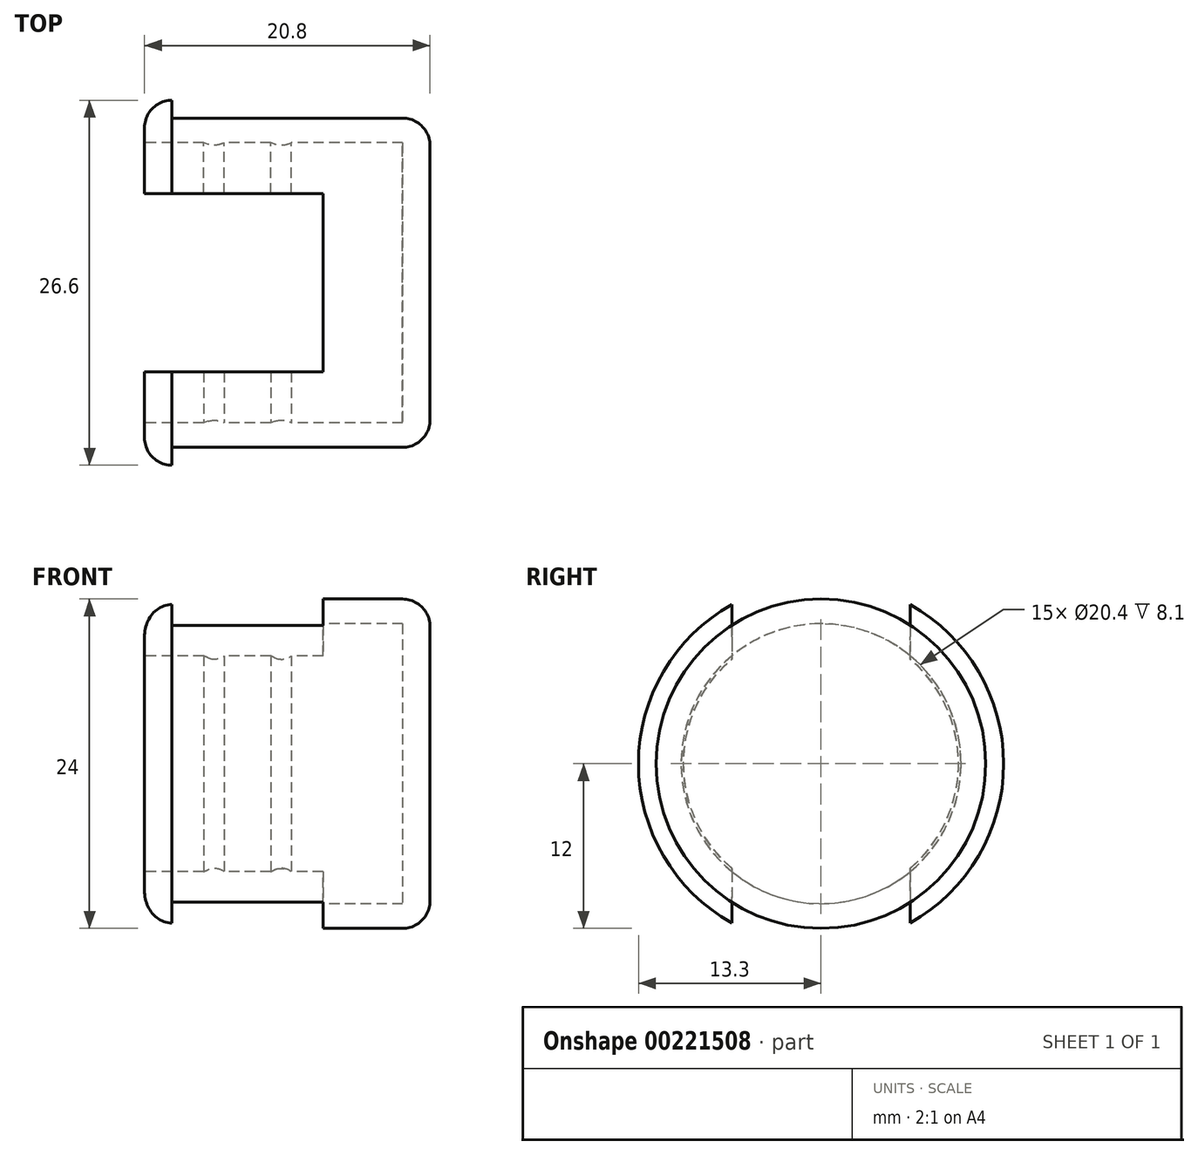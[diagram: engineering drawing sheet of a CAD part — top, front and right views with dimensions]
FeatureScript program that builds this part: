
annotation { "Feature Type Name" : "Feature", "Feature Type Description" : "" }
export const myFeature = defineFeature(function(context is Context, id is Id, definition is map)
    precondition{}
    {
        {
            var Q0;
            Q0=qCreatedBy(makeId("Front.planeOp"),FACE);
            var sketch = newSketch(context, id + "F3", { "sketchPlane" : qUnion([Q0])});
            skLineSegment(sketch, "E0", {"start": v(0, 0) * mm, "end": v(0, 12) * mm});
            skLineSegment(sketch, "E1", {"start": v(0, 12) * mm, "end": v(-18.8, 12) * mm});
            skLineSegment(sketch, "E2", {"start": v(-18.8, 12) * mm, "end": v(-18.8, 13.3) * mm});
            skLineSegment(sketch, "E3", {"start": v(-18.8, 13.3) * mm, "end": v(-20.8, 13.3) * mm});
            skLineSegment(sketch, "E4", {"start": v(-20.8, 13.3) * mm, "end": v(-20.8, 10.2) * mm});
            skLineSegment(sketch, "E5", {"start": v(-20.8, 10.2) * mm, "end": v(-2, 10.2) * mm});
            skLineSegment(sketch, "E6", {"start": v(-2, 10.2) * mm, "end": v(-2, 0) * mm});
            skLineSegment(sketch, "E7", {"start": v(-2, 0) * mm, "end": v(0, 0) * mm});
            skLineSegment(sketch, "E8", {"start": v(-16.5, 10.2) * mm, "end": v(-14.95, 9.7) * mm});
            skLineSegment(sketch, "E9", {"start": v(-14.95, 9.7) * mm, "end": v(-15, 10.2) * mm});
            skLineSegment(sketch, "E10", {"start": v(-11.6, 10.2) * mm, "end": v(-10.3, 9.7) * mm});
            skLineSegment(sketch, "E11", {"start": v(-10.3, 9.7) * mm, "end": v(-10.1, 10.2) * mm});
            skSolve(sketch);
        }
        {
            var Q0;
            Q0=makeQuery(id+"F3.imprint","IMPRINT",FACE,{"disambiguationData":[TD([[makeQuery(id+"F3.imprint","IMPRINT",EDGE,{"derivedFrom":sQuery(id+"F3.wireOp",EDGE,"E0")}),1.0]])]});
            var Q1;
            {var subQ0=sQuery(id+"F3.wireOp",EDGE,"E8");Q1=makeQuery(id+"F3.imprint","IMPRINT",FACE,{"disambiguationData":[TD([[makeQuery(id+"F3.imprint","IMPRINT",EDGE,{"derivedFrom":subQ0}),1.0]])]});}
            var Q2;
            {var subQ0=sQuery(id+"F3.wireOp",EDGE,"E10");Q2=makeQuery(id+"F3.imprint","IMPRINT",FACE,{"disambiguationData":[TD([[makeQuery(id+"F3.imprint","IMPRINT",EDGE,{"derivedFrom":subQ0}),1.0]])]});}
            var Q3;
            Q3=sQuery(id+"F3.wireOp",EDGE,"E7");
            revolve(context, id + "F0", {"entities" : qUnion([Q0, Q1, Q2]), "axis" : qUnion([Q3]), "revolveType" : RevolveType.FULL});
        }
        {
            var Q0;
            Q0=makeQuery(id+"F0.opRevolve","SWEPT_EDGE",EDGE,{"disambiguationData":[OSD([sQuery(id+"F3.wireOp",EDGE,"E3"),sQuery(id+"F3.wireOp",EDGE,"E4")])]});
            fillet(context, id + "F1", {"entities" : qUnion([Q0]), "radius" : 2 * mm, "tangentPropagation" : true, "allowEdgeOverflow" : false});
        }
        {
            var Q0;
            Q0=makeQuery(id+"F0.opRevolve","SWEPT_EDGE",EDGE,{"disambiguationData":[OSD([sQuery(id+"F3.wireOp",EDGE,"E8"),sQuery(id+"F3.wireOp",EDGE,"E9")])]});
            var Q1;
            Q1=makeQuery(id+"F0.opRevolve","SWEPT_EDGE",EDGE,{"disambiguationData":[OSD([sQuery(id+"F3.wireOp",EDGE,"E10"),sQuery(id+"F3.wireOp",EDGE,"E11")])]});
            fillet(context, id + "F4", {"entities" : qUnion([Q0, Q1]), "radius" : 1.5 * mm, "tangentPropagation" : true, "allowEdgeOverflow" : false});
        }
        {
            var Q0;
            Q0=qCreatedBy(makeId("Top.planeOp"),FACE);
            var sketch = newSketch(context, id + "F5", { "sketchPlane" : qUnion([Q0])});
            skLineSegment(sketch, "E12", {"start": v(-30.98, 6.5) * mm, "end": v(-7.8, 6.5) * mm});
            skLineSegment(sketch, "E13", {"start": v(-7.8, 6.5) * mm, "end": v(-7.8, -6.5) * mm});
            skLineSegment(sketch, "E14", {"start": v(-7.8, -6.5) * mm, "end": v(-30.89, -6.5) * mm});
            skLineSegment(sketch, "E15", {"start": v(-30.98, 6.5) * mm, "end": v(-30.89, -6.5) * mm});
            skSolve(sketch);
        }
        {
            var Q0;
            Q0=makeQuery(id+"F5.imprint","IMPRINT",FACE,{"disambiguationData":[TD([[makeQuery(id+"F5.imprint","IMPRINT",EDGE,{"derivedFrom":sQuery(id+"F5.wireOp",EDGE,"E12")}),-1.0]])]});
            extrude(context, id + "F2", {"entities" : qUnion([Q0]), "operationType" : NewBodyOperationType.REMOVE, "endBound" : BoundingType.SYMMETRIC, "depth" : 50 * mm});
        }
        {
            var Q0;
            Q0=makeQuery(id+"F0.opRevolve","SWEPT_EDGE",EDGE,{"disambiguationData":[OSD([sQuery(id+"F3.wireOp",EDGE,"E0"),sQuery(id+"F3.wireOp",EDGE,"E1")])]});
            fillet(context, id + "F6", {"entities" : qUnion([Q0]), "radius" : 2 * mm, "tangentPropagation" : true, "allowEdgeOverflow" : false});
        }
    });
